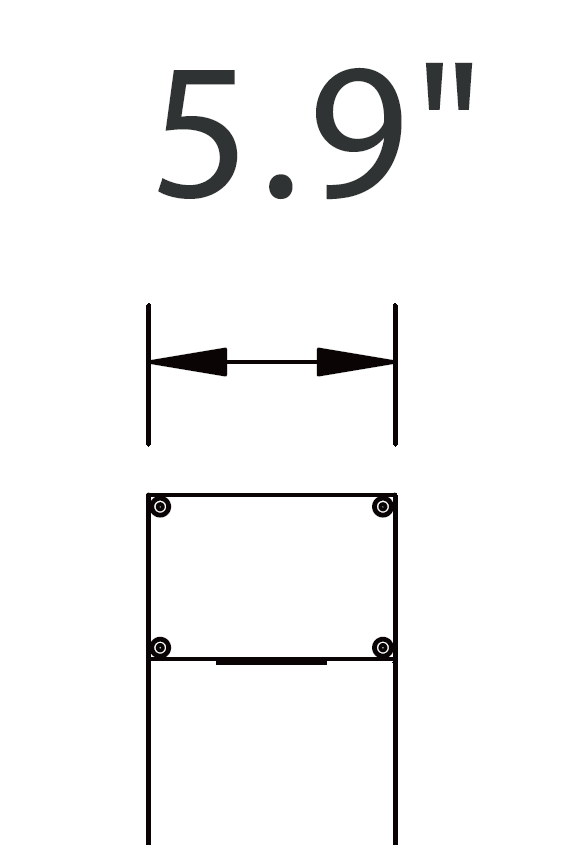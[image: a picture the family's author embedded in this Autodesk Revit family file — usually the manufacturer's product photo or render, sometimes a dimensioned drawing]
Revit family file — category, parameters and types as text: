
# Revit family: Lin2-9.84ft
name_source: partatom
category: Lighting Fixtures
units: mm (PartAtom-declared; Revit-internal decimal feet)

## family parameters
Always vertical = Yes
Cut with Voids When Loaded = No
Light Source = Yes
Maintain Annotation Orientation = No
OmniClass Number = 23.80.70.00
OmniClass Title = Lighting
Part Type = Normal
Room Calculation Point = No
Round Connector Dimension = Use Diameter
Shared = No
Work Plane-Based = No

## types (16) — shared parameters
CRI = 80
Color Filter = 16777215
Default Elevation = 0' - 0"
Dimming Lamp Color Temperature Shift = <None>
H = 9' - 10 3/32"
IP Rating = IP65
Input Voltage = 120-277V
Lamp = LED
Load Classification = Lighting
Manufacturer = Above All Lighting
Power Factor = 0.9
Tilt Angle = 90.00°
URL = https://www.abovealllighting.com

## per-type parameters (varying)
| type | Model | Photometric Web File | Wattage Comments |
| LIN2-70W-3000K-II-9.84ft | LIN2-7030801-II-BK | LIN2-7030801-II-BK.IES | 70W |
| LIN2-70W-3000K-III-9.84ft | LIN2-7030801-III-BK | LIN2-7030801-III-BK.IES | 70W |
| LIN2-70W-3000K-IV-9.84ft | LIN2-7030801-IV-BK | LIN2-7030801-IV-BK.IES | 70W |
| LIN2-70W-3000K-V-9.84ft | LIN2-7030801-V-BK | LIN2-7030801-V-BK.IES | 70W |
| LIN2-80W-3000K-II-9.84ft | LIN2-8030801-II-BK | LIN2-8030801-II-BK.IES | 80W |
| LIN2-80W-3000K-III-9.84ft | LIN2-8030801-III-BK | LIN2-8030801-III-BK.IES | 80W |
| LIN2-80W-3000K-IV-9.84ft | LIN2-8030801-IV-BK | LIN2-8030801-IV-BK.IES | 80W |
| LIN2-80W-3000K-V-9.84ft | LIN2-8030801-V-BK | LIN2-8030801-V-BK.IES | 80W |
| LIN2-100W-3000K-II-9.84ft | LIN2-10030801-II-BK | LIN2-10030801-II-BK.IES | 100W |
| LIN2-100W-3000K-III-9.84ft | LIN2-10030801-III-BK | LIN2-10030801-III-BK.IES | 100W |
| LIN2-100W-3000K-IV-9.84ft | LIN2-10030801-IV-BK | LIN2-10030801-IV-BK.IES | 100W |
| LIN2-100W-3000K-V-9.84ft | LIN2-10030801-V-BK | LIN2-10030801-V-BK.IES | 100W |
| LIN2-120W-3000K-II-9.84ft | LIN2-12030801-II-BK | LIN2-12030801-II-BK.IES | 120W |
| LIN2-120W-3000K-III-9.84ft | LIN2-12030801-III-BK | LIN2-12030801-III-BK.IES | 120W |
| LIN2-120W-3000K-IV-9.84ft | LIN2-12030801-IV-BK | LIN2-12030801-IV-BK.IES | 120W |
| LIN2-120W-3000K-V-9.84ft | LIN2-12030801-V-BK | LIN2-12030801-V-BK.IES | 120W |

## geometry (parser evidence)
native form markers: Sweep x2
no freeform markers — native parametric forms only
